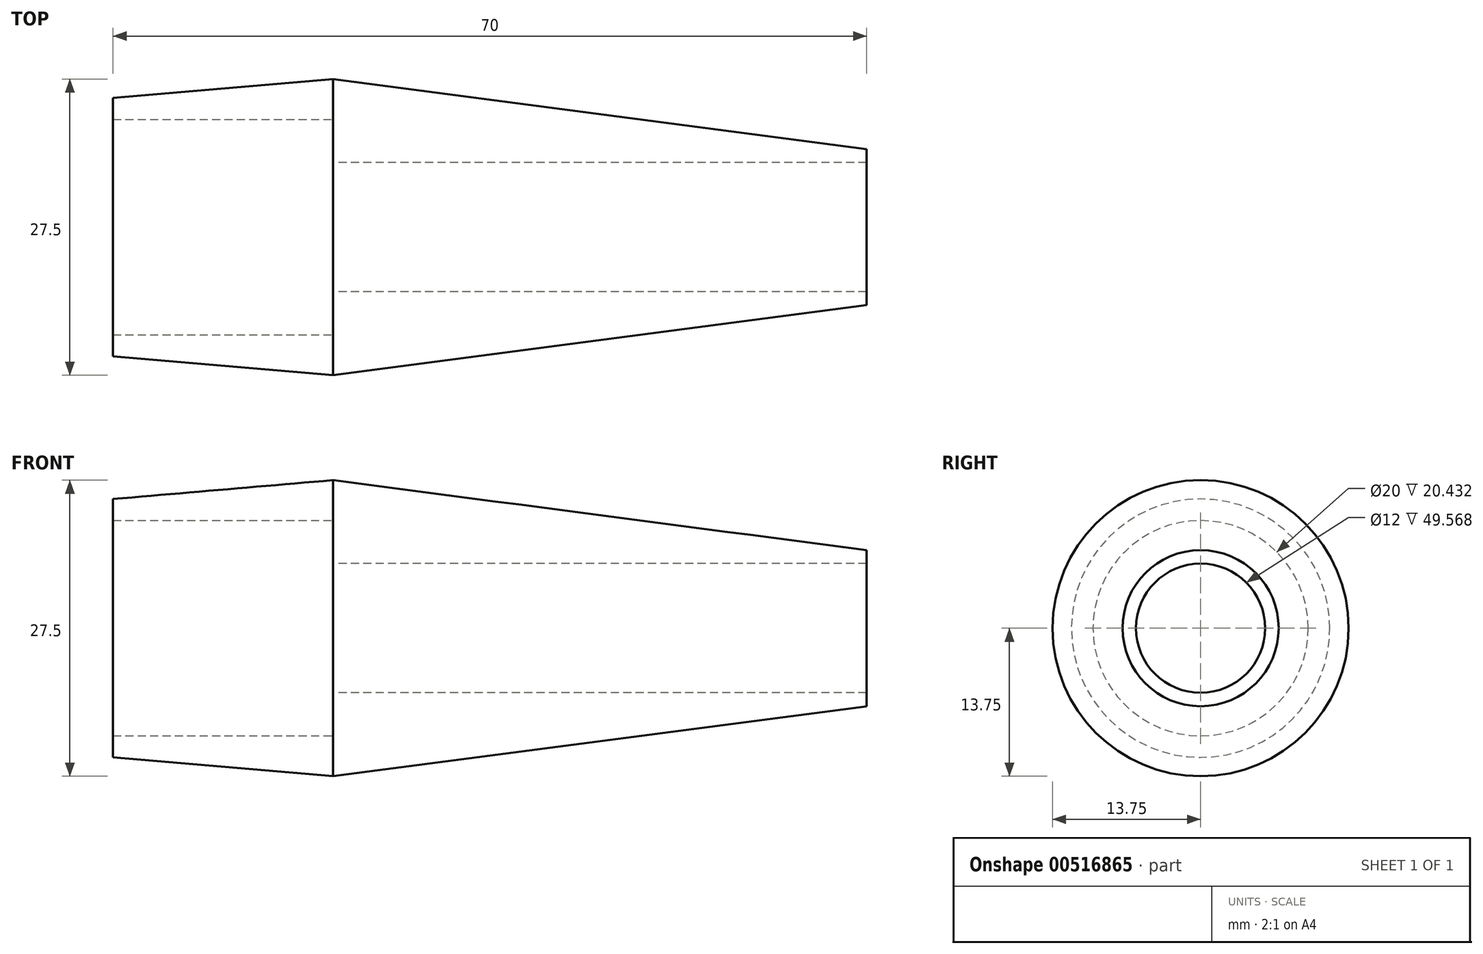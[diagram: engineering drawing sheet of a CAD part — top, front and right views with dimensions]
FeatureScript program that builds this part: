
annotation { "Feature Type Name" : "Feature", "Feature Type Description" : "" }
export const myFeature = defineFeature(function(context is Context, id is Id, definition is map)
    precondition{}
    {
        {
            var Q0;
            Q0=qCreatedBy(makeId("Top.planeOp"),FACE);
            var sketch = newSketch(context, id + "F0", { "sketchPlane" : qUnion([Q0])});
            skArc(sketch, "E0", {"start": v(0, 13) * mm, "mid": v(-13, 0) * mm, "end": v(0, -13) * mm});
            skLineSegment(sketch, "E1", {"start": v(0, 13) * mm, "end": v(0, -13) * mm});
            skSolve(sketch);
        }
        {
            var Q0;
            Q0=makeQuery(id+"F0.imprint","IMPRINT",FACE,{"disambiguationData":[TD([[makeQuery(id+"F0.imprint","IMPRINT",EDGE,{"derivedFrom":sQuery(id+"F0.wireOp",EDGE,"E0")}),1.0]])]});
            var Q1;
            Q1=sQuery(id+"F0.wireOp",EDGE,"E1");
            revolve(context, id + "F1", {"entities" : qUnion([Q0]), "axis" : qUnion([Q1]), "revolveType" : RevolveType.FULL});
        }
        {
            var Q0;
            Q0=qCreatedBy(makeId("Top.planeOp"),FACE);
            var Q1;
            Q1=qCreatedBy(makeId("Top.planeOp"),FACE);
            var sketch = newSketch(context, id + "F2", { "sketchPlane" : qUnion([Q0, Q1])});
            skCircle(sketch, "E2", {"center": v(0, 0) * mm, "radius": 10 * mm});
            skSolve(sketch);
        }
        {
            var Q0;
            Q0 = qSketchRegion(id + "F2", true);
            extrude(context, id + "F3", {"entities" : qUnion([Q0]), "operationType" : NewBodyOperationType.REMOVE, "endBound" : BoundingType.THROUGH_ALL, "depth" : 25 * mm, "offsetDistance" : 25 * mm});
        }
        {
            var Q0;
            Q0 = qSketchRegion(id + "F2", true);
            extrude(context, id + "F4", {"entities" : qUnion([Q0]), "operationType" : NewBodyOperationType.REMOVE, "oppositeDirection" : true, "depth" : 25 * mm, "offsetDistance" : 25 * mm});
        }
        {
            var Q0;
            Q0=qCreatedBy(makeId("Top.planeOp"),FACE);
            var sketch = newSketch(context, id + "F5", { "sketchPlane" : qUnion([Q0])});
            skLineSegment(sketch, "E3", {"start": v(0, -13.75) * mm, "end": v(49.57, -7.25) * mm});
            skLineSegment(sketch, "E4", {"start": v(0, -13.75) * mm, "end": v(-20.43, -12) * mm});
            skLineSegment(sketch, "E5", {"start": v(-20.43, -12) * mm, "end": v(-20.43, 0) * mm});
            skLineSegment(sketch, "E6", {"start": v(-20.43, 0) * mm, "end": v(49.57, 0) * mm});
            skLineSegment(sketch, "E7", {"start": v(49.57, 0) * mm, "end": v(49.57, -7.25) * mm});
            skSolve(sketch);
        }
        {
            var Q0;
            Q0 = qSketchRegion(id + "F5", true);
            var Q1;
            Q1=sQuery(id+"F5.wireOp",EDGE,"E6");
            revolve(context, id + "F6", {"operationType" : NewBodyOperationType.ADD, "entities" : qUnion([Q0]), "axis" : qUnion([Q1]), "revolveType" : RevolveType.FULL});
        }
        {
            var Q0;
            Q0=qCreatedBy(makeId("Right.planeOp"),FACE);
            var sketch = newSketch(context, id + "F7", { "sketchPlane" : qUnion([Q0])});
            skCircle(sketch, "E8", {"center": v(0, 0) * mm, "radius": 10 * mm});
            skSolve(sketch);
        }
        {
            var Q0;
            Q0 = qSketchRegion(id + "F7", true);
            extrude(context, id + "F8", {"entities" : qUnion([Q0]), "operationType" : NewBodyOperationType.REMOVE, "oppositeDirection" : true, "depth" : 50 * mm, "offsetDistance" : 25 * mm});
        }
        {
            var Q0;
            Q0=qCreatedBy(makeId("Right.planeOp"),FACE);
            var sketch = newSketch(context, id + "F9", { "sketchPlane" : qUnion([Q0])});
            skCircle(sketch, "E9", {"center": v(0, 0) * mm, "radius": 6 * mm});
            skSolve(sketch);
        }
        {
            var Q0;
            Q0 = qSketchRegion(id + "F9", true);
            extrude(context, id + "F10", {"entities" : qUnion([Q0]), "operationType" : NewBodyOperationType.REMOVE, "depth" : 75.4 * mm, "offsetDistance" : 25 * mm});
        }
    });
